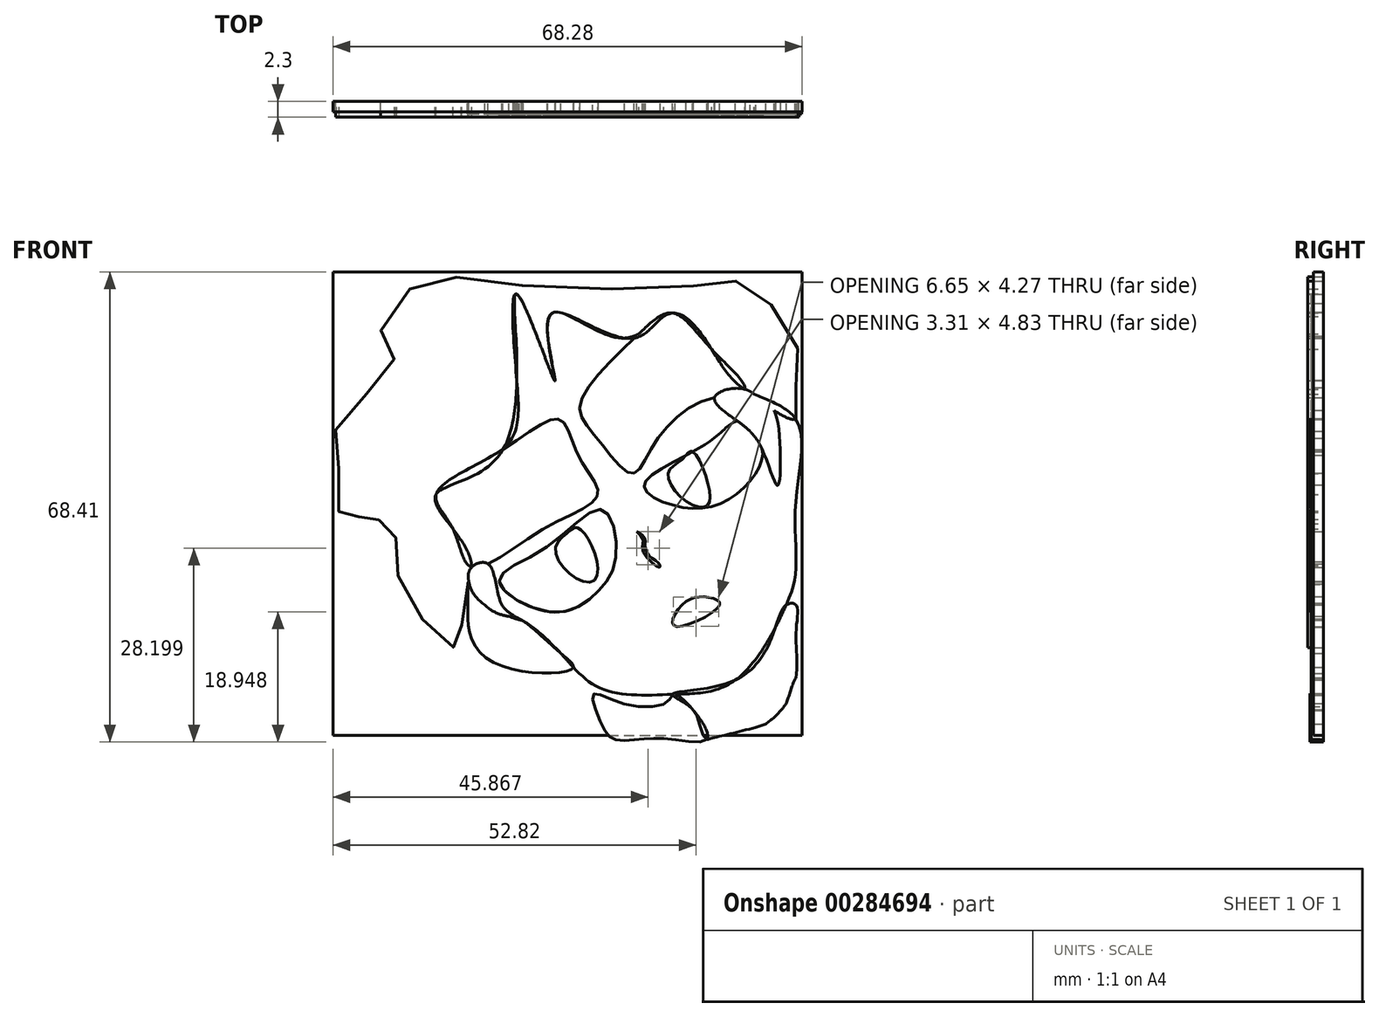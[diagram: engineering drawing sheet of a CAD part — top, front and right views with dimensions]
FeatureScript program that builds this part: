
annotation { "Feature Type Name" : "Feature", "Feature Type Description" : "" }
export const myFeature = defineFeature(function(context is Context, id is Id, definition is map)
    precondition{}
    {
        {
            var Q0;
            Q0=qCreatedBy(makeId("Front.planeOp"),FACE);
            var sketch = newSketch(context, id + "F0", { "sketchPlane" : qUnion([Q0])});
            skPoint(sketch, "E0.3.internal.snap0", {"position": v(-41.18, 8.07) * mm});
            skFitSpline(sketch, "E0", {"points": [v(-41.18, 21.35) * mm, v(-41.18, 16.35) * mm, v(-41.18, 8.07) * mm, v(-39.04, 8.07) * mm, v(-37.52, 6.33) * mm, v(-34.94, 6.94) * mm, v(-32.97, 4.66) * mm, v(-32.51, -1.56) * mm, v(-26.44, -10.35) * mm, v(-23.71, -11.57) * mm, v(-23.26, -5.5) * mm, v(-21.9, 0) * mm, v(-24.62, 5.57) * mm, v(-27.05, 10.58) * mm, v(-17.34, 17.1) * mm, v(-15.52, 39.7) * mm, v(-11.88, 32.28) * mm, v(-9.76, 27.12) * mm, v(-10.82, 33.64) * mm, v(-9.6, 37.13) * mm, v(1.77, 33.34) * mm, v(7.39, 36.98) * mm, v(15.28, 28.48) * mm, v(17.86, 25.9) * mm, v(25.31, 21.5) * mm, v(25.31, 26.2) * mm, v(25.31, 32.73) * mm, v(18, 41.18) * mm, v(12.85, 41.18) * mm, v(-16.43, 41.18) * mm, v(-29.78, 41.18) * mm, v(-35.1, 33.19) * mm, v(-33.12, 29.7) * mm, v(-41.18, 21.35) * mm]});
            skFitSpline(sketch, "E1", {"points": [v(-27.05, 10.58) * mm, v(-24.62, 5.57) * mm, v(-21.9, 0) * mm, v(-11.42, 5.57) * mm, v(-3.54, 10.58) * mm, v(-6.27, 16.04) * mm, v(-9.15, 21.5) * mm, v(-17.34, 17.1) * mm, v(-27.05, 10.58) * mm]});
            skFitSpline(sketch, "E2", {"points": [v(-6.11, 23.63) * mm, v(-3.54, 18.62) * mm, v(1.47, 13.62) * mm, v(4.5, 17.71) * mm, v(12.4, 24.39) * mm, v(17.86, 25.9) * mm, v(13.03, 31.73) * mm, v(7.39, 36.98) * mm, v(1.77, 33.34) * mm, v(-6.11, 23.63) * mm]});
            skFitSpline(sketch, "E3", {"points": [v(13.46, 24.67) * mm, v(16.82, 21.26) * mm, v(20.35, 17.24) * mm, v(22.56, 11.9) * mm, v(23.04, 14.8) * mm, v(22.1, 22.82) * mm, v(20.86, 23.66) * mm, v(17.86, 25.9) * mm, v(13.46, 24.67) * mm]});
            skFitSpline(sketch, "E4", {"points": [v(-22.3, -2.1) * mm, v(-19.94, -5.5) * mm, v(-14.5, -7.76) * mm, v(-17.5, -5.5) * mm, v(-19.5, 0.46) * mm, v(-21.9, 0) * mm, v(-22.3, -2.1) * mm]});
            skFitSpline(sketch, "E5", {"points": [v(-9.68, 2.89) * mm, v(-7.63, -0.98) * mm, v(-4.21, -2.04) * mm, v(-3.68, 1.07) * mm, v(-5.58, 5.01) * mm, v(-6.72, 5.77) * mm, v(-7.86, 5.09) * mm, v(-9.68, 2.89) * mm]});
            skFitSpline(sketch, "E6", {"points": [v(-17.87, -2.04) * mm, v(-11.04, 2.89) * mm, v(-2.85, 8.35) * mm, v(-0.88, 1.68) * mm, v(-3.76, -3.79) * mm, v(-10.36, -6.52) * mm, v(-17.87, -2.04) * mm]});
            skFitSpline(sketch, "E7", {"points": [v(6.7, 13.74) * mm, v(9.21, 9.64) * mm, v(12.4, 8.96) * mm, v(12.4, 12.52) * mm, v(10.12, 16.85) * mm, v(8.68, 15.63) * mm, v(6.7, 13.74) * mm]});
            skFitSpline(sketch, "E8", {"points": [v(3.22, 12) * mm, v(12.4, 18.06) * mm, v(16.82, 21.26) * mm, v(18.62, 19.8) * mm, v(20.35, 17.24) * mm, v(19.68, 14.04) * mm, v(14.83, 9.49) * mm, v(7.62, 8.96) * mm, v(3.22, 12) * mm]});
            skFitSpline(sketch, "E9", {"points": [v(2.15, 5.17) * mm, v(3.01, 4.15) * mm, v(3.01, 2.43) * mm, v(5.44, 0) * mm, v(5.44, 0.49) * mm, v(4.03, 1.54) * mm, v(3.33, 3.1) * mm, v(3.2, 4.4) * mm, v(2.15, 5.17) * mm]});
            skFitSpline(sketch, "E10", {"points": [v(8.73, -5.5) * mm, v(7.62, -8.56) * mm, v(14.18, -5.5) * mm, v(12.4, -4.35) * mm, v(8.73, -5.5) * mm]});
            skFitSpline(sketch, "E11", {"points": [v(-14.5, -7.76) * mm, v(-8.9, -12.57) * mm, v(-2.95, -17.71) * mm, v(7.33, -18.52) * mm, v(16.5, -16.43) * mm, v(23.9, -5.5) * mm, v(25.31, 0) * mm, v(25.31, 9.93) * mm, v(25.31, 21.5) * mm, v(17.86, 25.9) * mm, v(13.03, 31.73) * mm, v(7.39, 36.98) * mm, v(0.37, 33.34) * mm, v(-9.6, 37.13) * mm, v(-10.82, 33.64) * mm, v(-9.76, 27.12) * mm, v(-11.88, 32.28) * mm, v(-15.52, 39.7) * mm, v(-15.32, 27.12) * mm, v(-17.34, 17.1) * mm, v(-27.05, 10.58) * mm, v(-24.62, 5.57) * mm, v(-21.9, 0) * mm, v(-19.5, 0.46) * mm, v(-17.5, -5.5) * mm, v(-14.5, -7.76) * mm]});
            skFitSpline(sketch, "E12", {"points": [v(-22.43, -3.97) * mm, v(-22.43, -7.7) * mm, v(-20.28, -12.8) * mm, v(-10.92, -15.44) * mm, v(-7.1, -14.54) * mm, v(-8.9, -12.57) * mm, v(-14.5, -7.76) * mm, v(-16.45, -7.16) * mm, v(-19.94, -5.5) * mm, v(-22.3, -2.1) * mm, v(-22.43, -3.97) * mm]});
            skFitSpline(sketch, "E13", {"points": [v(7.33, -18.52) * mm, v(10.4, -20.87) * mm, v(12.34, -25.05) * mm, v(20.92, -22.8) * mm, v(25.31, -16.15) * mm, v(25.31, -9.4) * mm, v(25.31, -5.5) * mm, v(23.9, -5.5) * mm, v(22.33, -8.76) * mm, v(16.5, -16.43) * mm, v(7.33, -18.52) * mm]});
            skFitSpline(sketch, "E14", {"points": [v(12.34, -25.16) * mm, v(21.24, -25.05) * mm, v(25.31, -25.05) * mm, v(25.31, -21.73) * mm, v(25.31, -16.15) * mm, v(23.9, -19.81) * mm, v(20.92, -22.8) * mm, v(12.34, -25.16) * mm]});
            skFitSpline(sketch, "E15", {"points": [v(7.5, -18.5) * mm, v(6.65, -19.58) * mm, v(0, -19.8) * mm, v(-4.19, -18.52) * mm, v(-3, -22.8) * mm, v(-1.18, -25.05) * mm, v(2.57, -25.05) * mm, v(7.33, -25.05) * mm, v(12.34, -25.05) * mm, v(10.4, -20.87) * mm, v(7.5, -18.5) * mm]});
            skSolve(sketch);
        }
        {
            var Q0;
            {var subQ0=sQuery(id+"F0.wireOp",EDGE,"E11");var subQ1=sQuery(id+"F0.wireOp",EDGE,"E0");var subQ3=makeQuery(id+"F0.imprint","INTERSECT",VERTEX,{"disambiguationData":[OD(2.0)],"derivedFrom":[subQ1,subQ0]});Q0=makeQuery(id+"F0.imprint","IMPRINT",FACE,{"disambiguationData":[TD([[makeQuery(id+"F0.imprint","IMPRINT",EDGE,{"disambiguationData":[TD([[subQ3,-1.0]])],"derivedFrom":subQ1}),1.0]])]});}
            extrude(context, id + "F1", {"entities" : qUnion([Q0]), "depth" : 2.3 * mm});
        }
        {
            var Q0;
            {var subQ0=sQuery(id+"F0.wireOp",EDGE,"E11");var subQ1=sQuery(id+"F0.wireOp",EDGE,"E1");var subQ2=sQuery(id+"F0.wireOp",EDGE,"E0");var subQ7=makeQuery(id+"F0.imprint","INTERSECT",VERTEX,{"disambiguationData":[OD(1.0)],"derivedFrom":[subQ2,subQ1,subQ0]});Q0=makeQuery(id+"F0.imprint","IMPRINT",FACE,{"disambiguationData":[TD([[makeQuery(id+"F0.imprint","IMPRINT",EDGE,{"disambiguationData":[TD([[subQ7,-1.0]])],"derivedFrom":subQ2}),-1.0]])]});}
            var Q1;
            {var subQ1=sQuery(id+"F0.wireOp",EDGE,"E2");var subQ4=sQuery(id+"F0.wireOp",EDGE,"E0");var subQ7=makeQuery(id+"F0.imprint","INTERSECT",VERTEX,{"derivedFrom":[subQ4,subQ1]});Q1=makeQuery(id+"F0.imprint","IMPRINT",FACE,{"disambiguationData":[TD([[makeQuery(id+"F0.imprint","IMPRINT",EDGE,{"disambiguationData":[TD([[subQ7,-1.0]])],"derivedFrom":subQ4}),-1.0]])]});}
            extrude(context, id + "F2", {"entities" : qUnion([Q0, Q1]), "depth" : 2.3 * mm});
        }
        {
            var Q0;
            Q0=makeQuery(id+"F0.imprint","IMPRINT",FACE,{"disambiguationData":[TD([[makeQuery(id+"F0.imprint","IMPRINT",EDGE,{"derivedFrom":sQuery(id+"F0.wireOp",EDGE,"E6")}),1.0]])]});
            extrude(context, id + "F3", {"entities" : qUnion([Q0]), "depth" : 1.8 * mm});
        }
        {
            var Q0;
            {var subQ0=sQuery(id+"F0.wireOp",EDGE,"E8");var subQ1=sQuery(id+"F0.wireOp",EDGE,"E3");var subQ2=makeQuery(id+"F0.imprint","INTERSECT",VERTEX,{"disambiguationData":[OD(0.0)],"derivedFrom":[subQ1,subQ0]});Q0=makeQuery(id+"F0.imprint","IMPRINT",FACE,{"disambiguationData":[TD([[makeQuery(id+"F0.imprint","IMPRINT",EDGE,{"disambiguationData":[TD([[subQ2,-1.0]])],"derivedFrom":subQ1}),-1.0]])]});}
            var Q1;
            Q1=makeQuery(id+"F0.imprint","IMPRINT",FACE,{"disambiguationData":[TD([[makeQuery(id+"F0.imprint","IMPRINT",EDGE,{"derivedFrom":sQuery(id+"F0.wireOp",EDGE,"E5")}),-1.0]])]});
            extrude(context, id + "F4", {"entities" : qUnion([Q0, Q1]), "operationType" : NewBodyOperationType.ADD, "depth" : 2 * mm});
        }
        {
            var Q0;
            Q0=makeQuery(id+"F0.imprint","IMPRINT",FACE,{"disambiguationData":[TD([[makeQuery(id+"F0.imprint","IMPRINT",EDGE,{"derivedFrom":sQuery(id+"F0.wireOp",EDGE,"E5")}),1.0]])]});
            var Q1;
            {var subQ0=sQuery(id+"F0.wireOp",EDGE,"E8");var subQ1=sQuery(id+"F0.wireOp",EDGE,"E7");var subQ2=makeQuery(id+"F0.imprint","INTERSECT",VERTEX,{"disambiguationData":[OD(0.0)],"derivedFrom":[subQ1,subQ0]});Q1=makeQuery(id+"F0.imprint","IMPRINT",FACE,{"disambiguationData":[TD([[makeQuery(id+"F0.imprint","IMPRINT",EDGE,{"disambiguationData":[TD([[subQ2,1.0]])],"derivedFrom":subQ1}),1.0]])]});}
            extrude(context, id + "F5", {"entities" : qUnion([Q0, Q1]), "operationType" : NewBodyOperationType.ADD, "depth" : 2.3 * mm});
        }
        {
            var Q0;
            {var subQ0=sQuery(id+"F0.wireOp",EDGE,"E12");var subQ1=sQuery(id+"F0.wireOp",EDGE,"E11");var subQ2=makeQuery(id+"F0.imprint","INTERSECT",VERTEX,{"disambiguationData":[OD(0.0)],"derivedFrom":[subQ1,subQ0]});Q0=makeQuery(id+"F0.imprint","IMPRINT",FACE,{"disambiguationData":[TD([[makeQuery(id+"F0.imprint","IMPRINT",EDGE,{"disambiguationData":[TD([[subQ2,1.0]])],"derivedFrom":subQ1}),-1.0]])]});}
            var Q1;
            {var subQ0=sQuery(id+"F0.wireOp",EDGE,"E15");var subQ4=sQuery(id+"F0.wireOp",EDGE,"E11");var subQ12=makeQuery(id+"F0.imprint","INTERSECT",VERTEX,{"disambiguationData":[OD(1.0)],"derivedFrom":[subQ4,subQ0]});Q1=makeQuery(id+"F0.imprint","IMPRINT",FACE,{"disambiguationData":[TD([[makeQuery(id+"F0.imprint","IMPRINT",EDGE,{"disambiguationData":[TD([[subQ12,-1.0]])],"derivedFrom":subQ4}),-1.0]])]});}
            extrude(context, id + "F6", {"entities" : qUnion([Q0, Q1]), "depth" : 1.8 * mm});
        }
        {
            var Q0;
            {var subQ0=sQuery(id+"F0.wireOp",EDGE,"E15");var subQ1=sQuery(id+"F0.wireOp",EDGE,"E13");var subQ2=makeQuery(id+"F0.imprint","INTERSECT",VERTEX,{"disambiguationData":[OD(0.0)],"derivedFrom":[subQ1,subQ0]});Q0=makeQuery(id+"F0.imprint","IMPRINT",FACE,{"disambiguationData":[TD([[makeQuery(id+"F0.imprint","IMPRINT",EDGE,{"disambiguationData":[TD([[subQ2,-1.0]])],"derivedFrom":subQ1}),-1.0]])]});}
            extrude(context, id + "F7", {"entities" : qUnion([Q0]), "depth" : 2 * mm});
        }
        {
            var Q0;
            Q0=qCreatedBy(makeId("Front.planeOp"),FACE);
            var sketch = newSketch(context, id + "F8", { "sketchPlane" : qUnion([Q0])});
            skLineSegment(sketch, "E16.bottom", {"start": v(-42.06, 42.97) * mm, "end": v(26.22, 42.97) * mm});
            skLineSegment(sketch, "E16.top", {"start": v(-42.06, -24.47) * mm, "end": v(26.22, -24.47) * mm});
            skLineSegment(sketch, "E16.left", {"start": v(-42.06, 42.97) * mm, "end": v(-42.06, -24.47) * mm});
            skLineSegment(sketch, "E16.right", {"start": v(26.22, 42.97) * mm, "end": v(26.22, -24.47) * mm});
            skSolve(sketch);
        }
        {
            var Q0;
            Q0=makeQuery(id+"F8.imprint","IMPRINT",FACE,{"disambiguationData":[TD([[makeQuery(id+"F8.imprint","IMPRINT",EDGE,{"derivedFrom":sQuery(id+"F8.wireOp",EDGE,"E16.bottom")}),-1.0]])]});
            extrude(context, id + "F9", {"entities" : qUnion([Q0]), "depth" : 1.5 * mm});
        }
    });
